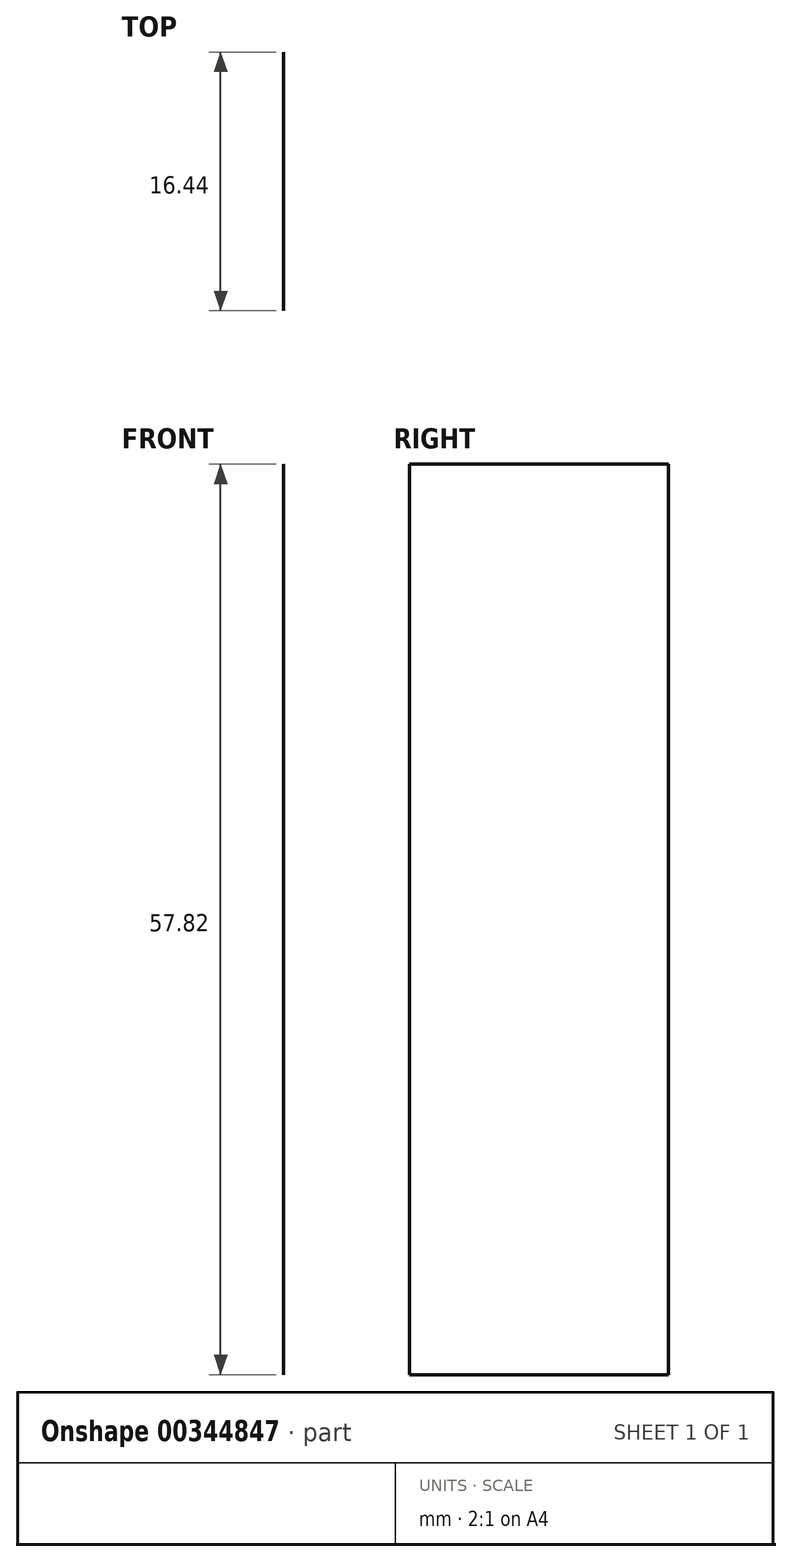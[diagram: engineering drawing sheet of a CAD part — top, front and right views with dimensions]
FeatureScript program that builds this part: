
annotation { "Feature Type Name" : "Feature", "Feature Type Description" : "" }
export const myFeature = defineFeature(function(context is Context, id is Id, definition is map)
    precondition{}
    {
        {
            var Q0;
            Q0=qCreatedBy(makeId("Front.planeOp"),FACE);
            var sketch = newSketch(context, id + "F0", { "sketchPlane" : qUnion([Q0])});
            skLineSegment(sketch, "E0.bottom", {"start": v(0, 0) * mm, "end": v(-38.68, 0) * mm});
            skLineSegment(sketch, "E0.top", {"start": v(0, 0) * mm, "end": v(-38.68, 0) * mm});
            skLineSegment(sketch, "E0.left", {"start": v(0, 0) * mm, "end": v(0, 0) * mm});
            skLineSegment(sketch, "E0.right", {"start": v(-38.68, 0) * mm, "end": v(-38.68, 0) * mm});
            skPoint(sketch, "E0.middle", {"position": v(-19.34, 0) * mm});
            skLineSegment(sketch, "E1.bottom", {"start": v(-38.68, 54.76) * mm, "end": v(-38.68, 54.76) * mm});
            skLineSegment(sketch, "E1.top", {"start": v(-38.68, 62.06) * mm, "end": v(-38.68, 62.06) * mm});
            skLineSegment(sketch, "E1.left", {"start": v(-38.68, 54.76) * mm, "end": v(-38.68, 62.06) * mm});
            skLineSegment(sketch, "E1.right", {"start": v(-38.68, 54.76) * mm, "end": v(-38.68, 62.06) * mm});
            skPoint(sketch, "E1.middle", {"position": v(-38.68, 58.41) * mm});
            skLineSegment(sketch, "E2.bottom", {"start": v(-22.45, 82.02) * mm, "end": v(34.04, 82.02) * mm});
            skLineSegment(sketch, "E2.top", {"start": v(-22.45, 24.2) * mm, "end": v(34.04, 24.2) * mm});
            skLineSegment(sketch, "E2.left", {"start": v(-22.45, 82.02) * mm, "end": v(-22.45, 24.2) * mm});
            skLineSegment(sketch, "E2.right", {"start": v(34.04, 82.02) * mm, "end": v(34.04, 24.2) * mm});
            skPoint(sketch, "E2.middle", {"position": v(5.8, 53.11) * mm});
            skLineSegment(sketch, "E3.bottom", {"start": v(5.8, 53.11) * mm, "end": v(-50.7, 53.11) * mm});
            skLineSegment(sketch, "E3.top", {"start": v(5.8, 75.36) * mm, "end": v(-50.7, 75.36) * mm});
            skLineSegment(sketch, "E3.left", {"start": v(5.8, 53.11) * mm, "end": v(5.8, 75.36) * mm});
            skLineSegment(sketch, "E3.right", {"start": v(-50.7, 53.11) * mm, "end": v(-50.7, 75.36) * mm});
            skPoint(sketch, "E3.middle", {"position": v(-22.45, 64.23) * mm});
            skLineSegment(sketch, "E4.bottom", {"start": v(20.7, 49.2) * mm, "end": v(6.34, 49.2) * mm});
            skLineSegment(sketch, "E4.top", {"start": v(20.7, 48.84) * mm, "end": v(6.34, 48.84) * mm});
            skLineSegment(sketch, "E4.left", {"start": v(20.7, 49.2) * mm, "end": v(20.7, 48.84) * mm});
            skLineSegment(sketch, "E4.right", {"start": v(6.34, 49.2) * mm, "end": v(6.34, 48.84) * mm});
            skPoint(sketch, "E4.middle", {"position": v(13.52, 49.02) * mm});
            skSolve(sketch);
        }
        {
            var Q0;
            {var subQ6=sQuery(id+"F0.wireOp",EDGE,"E2.bottom");Q0=makeQuery(id+"F0.imprint","IMPRINT",FACE,{"disambiguationData":[TD([[makeQuery(id+"F0.imprint","IMPRINT",EDGE,{"derivedFrom":subQ6}),-1.0]])]});}
            var Q1;
            Q1=sQuery(id+"F0.wireOp",EDGE,"E2.right");
            extrude(context, id + "F1", {"entities" : qUnion([Q0]), "bodyType" : ToolBodyType.SURFACE, "surfaceEntities" : qUnion([Q1]), "depth" : 16.44 * mm});
        }
    });
